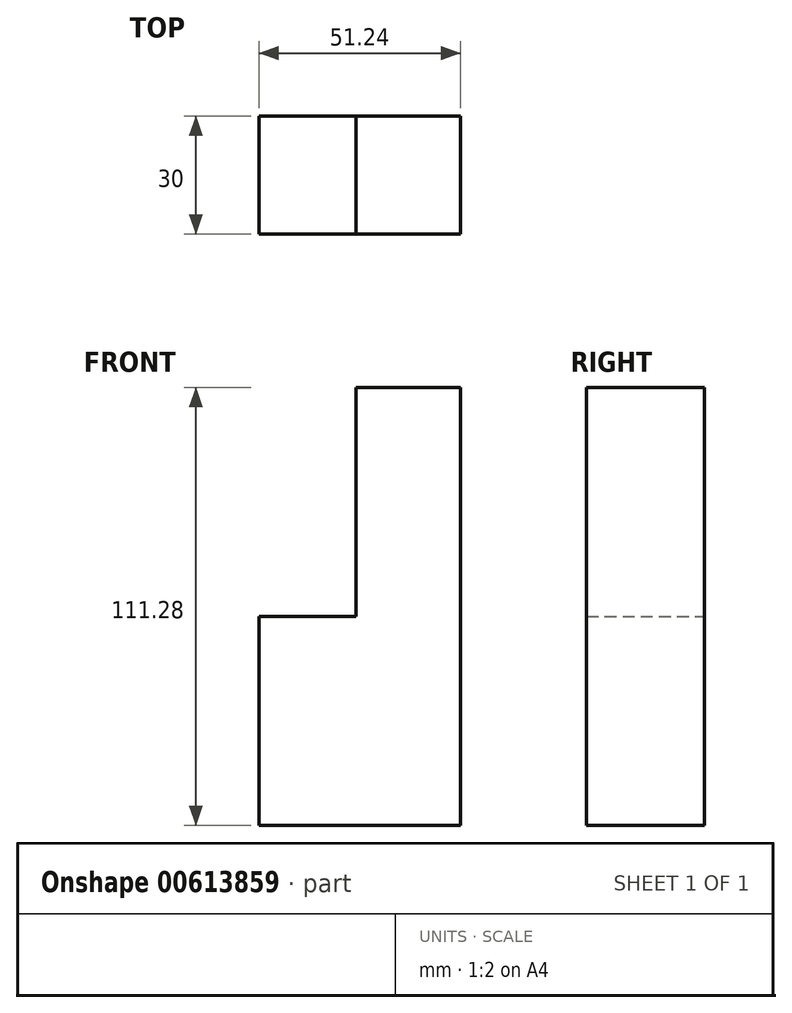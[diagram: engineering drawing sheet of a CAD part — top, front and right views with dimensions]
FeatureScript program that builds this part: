
annotation { "Feature Type Name" : "Feature", "Feature Type Description" : "" }
export const myFeature = defineFeature(function(context is Context, id is Id, definition is map)
    precondition{}
    {
        {
            var Q0;
            Q0=qCreatedBy(makeId("Front.planeOp"),FACE);
            var sketch = newSketch(context, id + "F0", { "sketchPlane" : qUnion([Q0])});
            skLineSegment(sketch, "E0.bottom", {"start": v(-26.57, 52.56) * mm, "end": v(0, 52.56) * mm});
            skLineSegment(sketch, "E0.left", {"start": v(-26.57, 52.56) * mm, "end": v(-26.57, -5.58) * mm});
            skLineSegment(sketch, "E0.right", {"start": v(0, 52.56) * mm, "end": v(0, -5.58) * mm});
            skLineSegment(sketch, "E1.bottom", {"start": v(-26.57, -5.58) * mm, "end": v(-51.24, -5.58) * mm});
            skLineSegment(sketch, "E1.top", {"start": v(0, -58.72) * mm, "end": v(-51.24, -58.72) * mm});
            skLineSegment(sketch, "E1.left", {"start": v(0, -5.58) * mm, "end": v(0, -58.72) * mm});
            skLineSegment(sketch, "E1.right", {"start": v(-51.24, -5.58) * mm, "end": v(-51.24, -58.72) * mm});
            skSolve(sketch);
        }
        {
            var Q0;
            Q0 = qSketchRegion(id + "F0", true);
            extrude(context, id + "F1", {"entities" : qUnion([Q0]), "depth" : 30 * mm, "offsetDistance" : 25 * mm});
        }
    });
